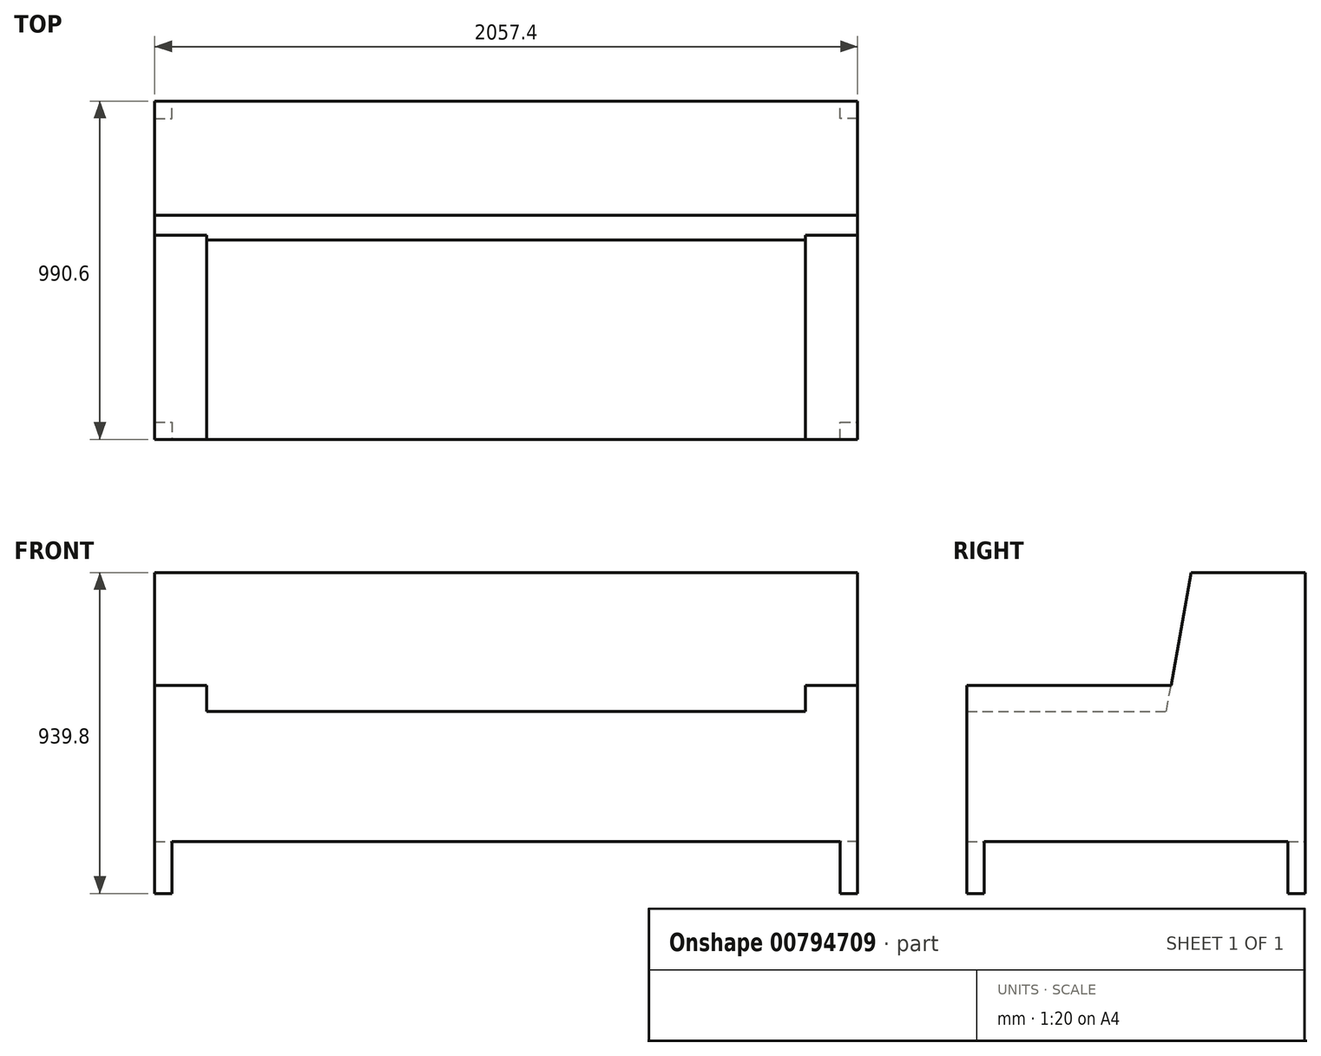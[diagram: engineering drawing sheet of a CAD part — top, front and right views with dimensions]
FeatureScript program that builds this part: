
annotation { "Feature Type Name" : "Feature", "Feature Type Description" : "" }
export const myFeature = defineFeature(function(context is Context, id is Id, definition is map)
    precondition{}
    {
        {
            var Q0;
            Q0=qCreatedBy(makeId("Top.planeOp"),FACE);
            var sketch = newSketch(context, id + "F0", { "sketchPlane" : qUnion([Q0])});
            skLineSegment(sketch, "E0.rect.bottom", {"start": v(-1028.7, 495.3) * mm, "end": v(1028.7, 495.3) * mm});
            skLineSegment(sketch, "E0.rect.top", {"start": v(-1028.7, -495.3) * mm, "end": v(1028.7, -495.3) * mm});
            skLineSegment(sketch, "E0.rect.left", {"start": v(-1028.7, 495.3) * mm, "end": v(-1028.7, -495.3) * mm});
            skLineSegment(sketch, "E0.rect.right", {"start": v(1028.7, 495.3) * mm, "end": v(1028.7, -495.3) * mm});
            skPoint(sketch, "E0.rect.middle", {"position": v(0, 0) * mm});
            skSolve(sketch);
        }
        {
            var Q0;
            Q0=makeQuery(id+"F0.imprint","IMPRINT",FACE,{"disambiguationData":[TD([[makeQuery(id+"F0.imprint","IMPRINT",EDGE,{"derivedFrom":sQuery(id+"F0.wireOp",EDGE,"E0.rect.bottom")}),-1.0]])]});
            extrude(context, id + "F1", {"entities" : qUnion([Q0]), "depth" : 939.8 * mm});
        }
        {
            var Q0;
            Q0=qCreatedBy(makeId("Right.planeOp"),FACE);
            var sketch = newSketch(context, id + "F2", { "sketchPlane" : qUnion([Q0])});
            skLineSegment(sketch, "E1", {"start": v(-495.3, 533.4) * mm, "end": v(88.9, 533.4) * mm});
            skLineSegment(sketch, "E2", {"start": v(88.9, 533.4) * mm, "end": v(160.56, 939.8) * mm});
            skLineSegment(sketch, "E3", {"start": v(160.56, 939.8) * mm, "end": v(-495.3, 939.8) * mm});
            skLineSegment(sketch, "E4", {"start": v(-495.3, 939.8) * mm, "end": v(-495.3, 533.4) * mm});
            skSolve(sketch);
        }
        {
            var Q0;
            Q0=makeQuery(id+"F2.imprint","IMPRINT",FACE,{"disambiguationData":[TD([[makeQuery(id+"F2.imprint","IMPRINT",EDGE,{"derivedFrom":sQuery(id+"F2.wireOp",EDGE,"E1")}),1.0]])]});
            extrude(context, id + "F3", {"entities" : qUnion([Q0]), "operationType" : NewBodyOperationType.REMOVE, "oppositeDirection" : true, "depth" : 1752.6 * mm, "symmetric" : true});
        }
        {
            var Q0;
            Q0=qCreatedBy(makeId("Right.planeOp"),FACE);
            var sketch = newSketch(context, id + "F4", { "sketchPlane" : qUnion([Q0])});
            skLineSegment(sketch, "E5", {"start": v(-495.3, 609.6) * mm, "end": v(102.34, 609.6) * mm});
            skLineSegment(sketch, "E6", {"start": v(160.56, 939.8) * mm, "end": v(102.34, 609.6) * mm});
            skLineSegment(sketch, "E7", {"start": v(160.56, 939.8) * mm, "end": v(-495.3, 939.8) * mm});
            skLineSegment(sketch, "E8", {"start": v(-495.3, 609.6) * mm, "end": v(-495.3, 939.8) * mm});
            skSolve(sketch);
        }
        {
            var Q0;
            Q0=makeQuery(id+"F4.imprint","IMPRINT",FACE,{"disambiguationData":[TD([[makeQuery(id+"F4.imprint","IMPRINT",EDGE,{"derivedFrom":sQuery(id+"F4.wireOp",EDGE,"E5")}),1.0]])]});
            extrude(context, id + "F5", {"entities" : qUnion([Q0]), "operationType" : NewBodyOperationType.REMOVE, "oppositeDirection" : true, "depth" : 254000 * mm, "symmetric" : true});
        }
        {
            var Q0;
            Q0=makeQuery(id+"F1.opExtrude","CAP_FACE",FACE,{"disambiguationData":[OSD([sQuery(id+"F0.wireOp",EDGE,"E0.rect.bottom"),sQuery(id+"F0.wireOp",EDGE,"E0.rect.top"),sQuery(id+"F0.wireOp",EDGE,"E0.rect.left"),sQuery(id+"F0.wireOp",EDGE,"E0.rect.right")])],"isStart":true});
            var sketch = newSketch(context, id + "F6", { "sketchPlane" : qUnion([Q0])});
            skLineSegment(sketch, "E9.bottom", {"start": v(-977.9, 495.3) * mm, "end": v(977.9, 495.3) * mm});
            skLineSegment(sketch, "E9.top", {"start": v(-977.9, -495.3) * mm, "end": v(977.9, -495.3) * mm});
            skLineSegment(sketch, "E9.left", {"start": v(-1028.7, 444.5) * mm, "end": v(-1028.7, -444.5) * mm});
            skLineSegment(sketch, "E9.right", {"start": v(1028.7, 444.5) * mm, "end": v(1028.7, -444.5) * mm});
            skLineSegment(sketch, "E10.bottom", {"start": v(-1028.7, 444.5) * mm, "end": v(-977.9, 444.5) * mm});
            skLineSegment(sketch, "E10.right", {"start": v(-977.9, 444.5) * mm, "end": v(-977.9, 495.3) * mm});
            skLineSegment(sketch, "E11.top", {"start": v(977.9, 444.5) * mm, "end": v(1028.7, 444.5) * mm});
            skLineSegment(sketch, "E11.left", {"start": v(977.9, 495.3) * mm, "end": v(977.9, 444.5) * mm});
            skLineSegment(sketch, "E12.bottom", {"start": v(1028.7, -444.5) * mm, "end": v(977.9, -444.5) * mm});
            skLineSegment(sketch, "E12.right", {"start": v(977.9, -444.5) * mm, "end": v(977.9, -495.3) * mm});
            skLineSegment(sketch, "E13.bottom", {"start": v(-1028.7, -444.5) * mm, "end": v(-977.9, -444.5) * mm});
            skLineSegment(sketch, "E13.right", {"start": v(-977.9, -444.5) * mm, "end": v(-977.9, -495.3) * mm});
            skSolve(sketch);
        }
        {
            var Q0;
            Q0=makeQuery(id+"F6.imprint","IMPRINT",FACE,{"disambiguationData":[TD([[makeQuery(id+"F6.imprint","IMPRINT",EDGE,{"derivedFrom":sQuery(id+"F6.wireOp",EDGE,"E9.bottom")}),-1.0]])]});
            extrude(context, id + "F7", {"entities" : qUnion([Q0]), "operationType" : NewBodyOperationType.REMOVE, "oppositeDirection" : true, "depth" : 152.4 * mm});
        }
    });
